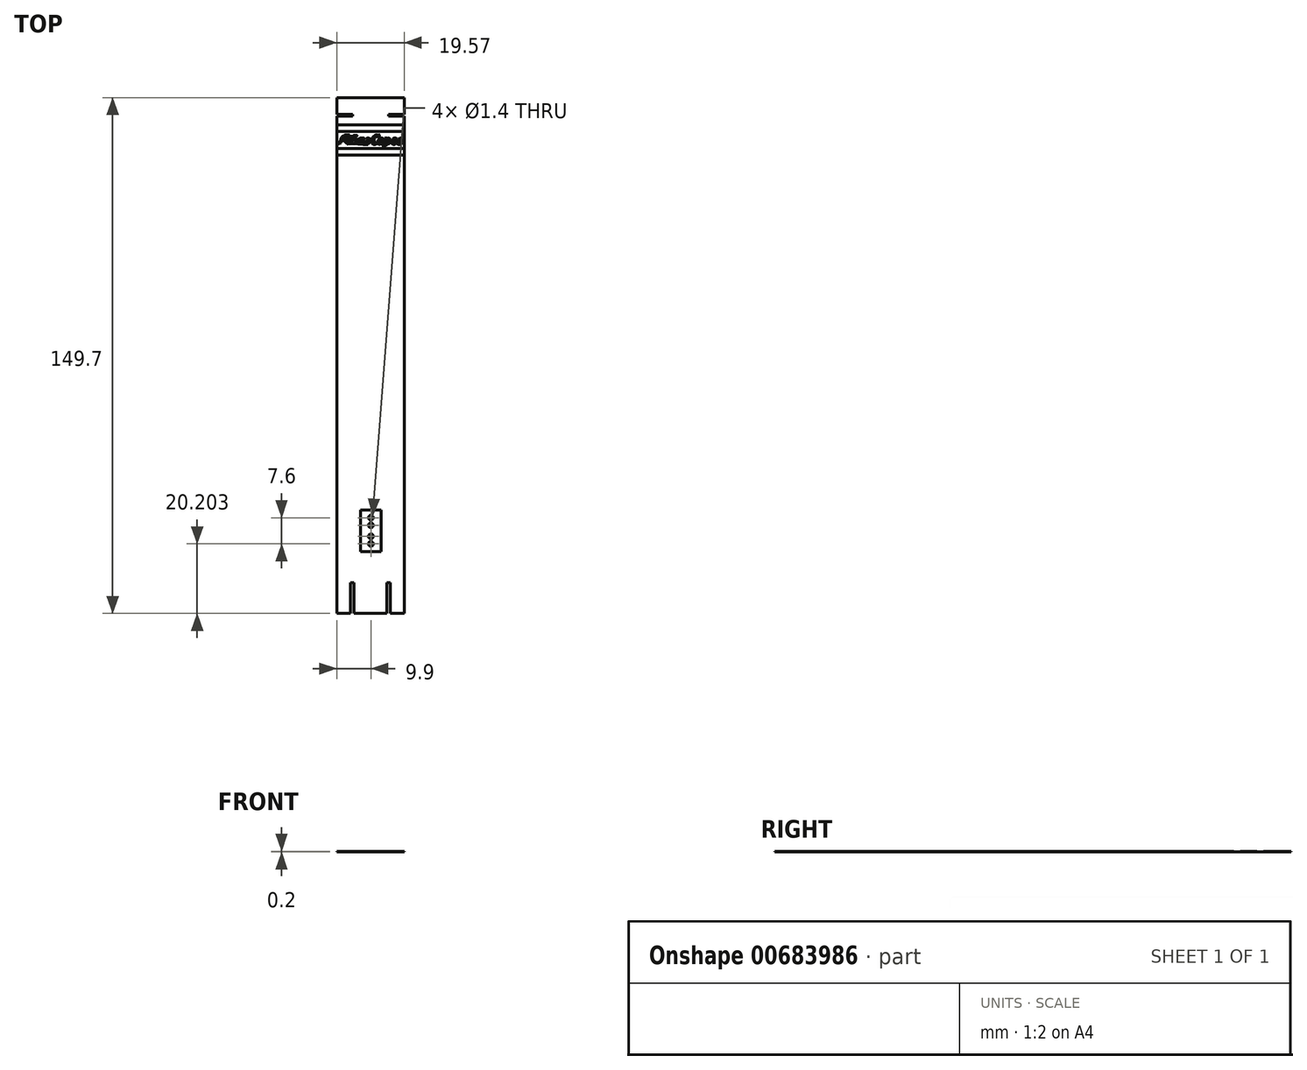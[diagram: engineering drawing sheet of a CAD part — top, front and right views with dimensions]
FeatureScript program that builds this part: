
annotation { "Feature Type Name" : "Feature", "Feature Type Description" : "" }
export const myFeature = defineFeature(function(context is Context, id is Id, definition is map)
    precondition{}
    {
        {
            var Q0;
            Q0=qCreatedBy(makeId("Top.planeOp"),FACE);
            var sketch = newSketch(context, id + "F0", { "sketchPlane" : qUnion([Q0])});
            skLineSegment(sketch, "E0.bottom", {"start": v(0, -51.23) * mm, "end": v(-19.57, -51.23) * mm});
            skLineSegment(sketch, "E0.top", {"start": v(0, 98.47) * mm, "end": v(-19.57, 98.47) * mm});
            skLineSegment(sketch, "E0.left", {"start": v(0, -51.23) * mm, "end": v(0, 98.47) * mm});
            skLineSegment(sketch, "E0.right", {"start": v(-19.57, -51.23) * mm, "end": v(-19.57, 98.47) * mm});
            skSolve(sketch);
        }
        {
            var Q0;
            Q0=makeQuery(id+"F0.imprint","IMPRINT",FACE,{"disambiguationData":[TD([[makeQuery(id+"F0.imprint","IMPRINT",EDGE,{"derivedFrom":sQuery(id+"F0.wireOp",EDGE,"E0.bottom")}),-1.0]])]});
            extrude(context, id + "F1", {"entities" : qUnion([Q0]), "depth" : 0.2 * mm, "offsetDistance" : 25 * mm});
        }
        {
            var Q0;
            Q0=makeQuery(id+"F1.opExtrude","CAP_FACE",FACE,{"disambiguationData":[OSD([sQuery(id+"F0.wireOp",EDGE,"E0.bottom"),sQuery(id+"F0.wireOp",EDGE,"E0.top"),sQuery(id+"F0.wireOp",EDGE,"E0.left"),sQuery(id+"F0.wireOp",EDGE,"E0.right")])],"isStart":false});
            var sketch = newSketch(context, id + "F2", { "sketchPlane" : qUnion([Q0])});
            skLineSegment(sketch, "E1", {"start": v(0, 90.56) * mm, "end": v(-19.57, 90.56) * mm});
            skLineSegment(sketch, "E2", {"start": v(-19.57, 90.56) * mm, "end": v(-19.57, 88.66) * mm});
            skLineSegment(sketch, "E3", {"start": v(-19.57, 88.66) * mm, "end": v(0, 88.66) * mm});
            skLineSegment(sketch, "E4", {"start": v(0, 88.66) * mm, "end": v(0, 90.56) * mm});
            skLineSegment(sketch, "E5", {"start": v(0, 88.66) * mm, "end": v(0, 83.76) * mm});
            skLineSegment(sketch, "E6", {"start": v(0, 83.76) * mm, "end": v(-19.57, 83.76) * mm});
            skLineSegment(sketch, "E7", {"start": v(-19.57, 83.76) * mm, "end": v(-19.57, 81.86) * mm});
            skLineSegment(sketch, "E8", {"start": v(-19.57, 81.86) * mm, "end": v(0, 81.86) * mm});
            skLineSegment(sketch, "E9", {"start": v(0, 81.86) * mm, "end": v(0, 83.76) * mm});
            skSolve(sketch);
        }
        {
            var Q0;
            Q0 = qSketchRegion(id + "F2", true);
            extrude(context, id + "F3", {"entities" : qUnion([Q0]), "operationType" : NewBodyOperationType.REMOVE, "oppositeDirection" : true, "depth" : 0.1 * mm, "offsetDistance" : 25 * mm});
        }
        {
            var Q0;
            {var subQ0=sQuery(id+"F0.wireOp",EDGE,"E0.top");var subQ1=sQuery(id+"F0.wireOp",EDGE,"E0.left");var subQ2=sQuery(id+"F0.wireOp",EDGE,"E0.right");Q0=makeQuery(id+"F3.boolean.opBoolean","SPLIT",FACE,{"disambiguationData":[TD([makeQuery(id+"F1.opExtrude","SWEPT_FACE",FACE,{"disambiguationData":[OSD([subQ0])]})])],"derivedFrom":makeQuery(id+"F1.opExtrude","CAP_FACE",FACE,{"disambiguationData":[OSD([sQuery(id+"F0.wireOp",EDGE,"E0.bottom"),subQ0,subQ1,subQ2])],"isStart":false})});}
            var sketch = newSketch(context, id + "F4", { "sketchPlane" : qUnion([Q0])});
            skLineSegment(sketch, "E10", {"start": v(0, 93.57) * mm, "end": v(-4.6, 93.57) * mm});
            skLineSegment(sketch, "E11", {"start": v(-4.6, 93.57) * mm, "end": v(-4.6, 93.07) * mm});
            skLineSegment(sketch, "E12", {"start": v(-4.6, 93.07) * mm, "end": v(0, 93.07) * mm});
            skLineSegment(sketch, "E13", {"start": v(-19.57, 93.57) * mm, "end": v(-14.97, 93.57) * mm});
            skLineSegment(sketch, "E14", {"start": v(-14.97, 93.57) * mm, "end": v(-14.97, 93.07) * mm});
            skLineSegment(sketch, "E15", {"start": v(-14.97, 93.07) * mm, "end": v(-19.57, 93.07) * mm});
            skLineSegment(sketch, "E16", {"start": v(-19.57, 93.57) * mm, "end": v(-19.57, 93.07) * mm});
            skLineSegment(sketch, "E17", {"start": v(0, 93.57) * mm, "end": v(0, 93.07) * mm});
            skSolve(sketch);
        }
        {
            var Q0;
            Q0=makeQuery(id+"F4.imprint","IMPRINT",FACE,{"disambiguationData":[TD([[makeQuery(id+"F4.imprint","IMPRINT",EDGE,{"derivedFrom":sQuery(id+"F4.wireOp",EDGE,"E13")}),-1.0]])]});
            var Q1;
            Q1=makeQuery(id+"F4.imprint","IMPRINT",FACE,{"disambiguationData":[TD([[makeQuery(id+"F4.imprint","IMPRINT",EDGE,{"derivedFrom":sQuery(id+"F4.wireOp",EDGE,"E10")}),1.0]])]});
            extrude(context, id + "F5", {"entities" : qUnion([Q0, Q1]), "operationType" : NewBodyOperationType.REMOVE, "oppositeDirection" : true, "depth" : 0.2 * mm, "offsetDistance" : 25 * mm});
        }
        {
            var Q0;
            {var subQ0=sQuery(id+"F0.wireOp",EDGE,"E0.left");var subQ1=sQuery(id+"F0.wireOp",EDGE,"E0.right");Q0=makeQuery(id+"F3.boolean.opBoolean","SPLIT",FACE,{"disambiguationData":[TD([makeQuery(id+"F3.opExtrude","SWEPT_FACE",FACE,{"disambiguationData":[OSD([sQuery(id+"F2.wireOp",EDGE,"E3")])]})])],"derivedFrom":makeQuery(id+"F1.opExtrude","CAP_FACE",FACE,{"disambiguationData":[OSD([sQuery(id+"F0.wireOp",EDGE,"E0.bottom"),sQuery(id+"F0.wireOp",EDGE,"E0.top"),subQ0,subQ1])],"isStart":false})});}
            var sketch = newSketch(context, id + "F6", { "sketchPlane" : qUnion([Q0])});
            skFitSpline(sketch, "E18", {"points": [v(-19.42, 85.15) * mm, v(-19.42, 84.95) * mm, v(-19.42, 84.87) * mm, v(-19.22, 84.83) * mm, v(-19.09, 84.82) * mm, v(-18.87, 84.84) * mm, v(-18.7, 84.9) * mm, v(-18.52, 84.98) * mm, v(-18.35, 85.1) * mm, v(-18.2, 85.24) * mm, v(-18.12, 85.38) * mm, v(-18, 85.53) * mm, v(-17.94, 85.73) * mm, v(-17.89, 85.92) * mm, v(-17.86, 86.08) * mm, v(-17.85, 86.1) * mm, v(-17.71, 86.1) * mm, v(-17.6, 86.1) * mm, v(-17.46, 86.1) * mm, v(-17.32, 86.08) * mm, v(-17.3, 86.08) * mm, v(-17.26, 86.1) * mm, v(-17.43, 85.47) * mm, v(-17.45, 85.37) * mm, v(-17.44, 85.2) * mm, v(-17.4, 85.1) * mm, v(-17.35, 85.01) * mm, v(-17.29, 84.94) * mm, v(-17.22, 84.9) * mm, v(-17.16, 84.87) * mm, v(-17.02, 84.84) * mm, v(-16.85, 84.84) * mm, v(-16.7, 84.84) * mm, v(-16.55, 84.88) * mm, v(-16.42, 84.92) * mm, v(-16.33, 85.01) * mm, v(-16.26, 85.07) * mm, v(-16.19, 85.15) * mm, v(-16.15, 85.18) * mm, v(-16.13, 85.19) * mm, v(-16.08, 85.1) * mm, v(-16.03, 84.97) * mm, v(-15.98, 84.9) * mm, v(-15.9, 84.84) * mm, v(-15.75, 84.84) * mm, v(-15.6, 84.83) * mm, v(-15.55, 84.83) * mm, v(-15.46, 84.85) * mm, v(-15.4, 84.88) * mm, v(-15.3, 84.91) * mm, v(-15.23, 84.94) * mm, v(-15.1, 85.04) * mm, v(-15, 85.1) * mm, v(-14.97, 85.17) * mm, v(-14.93, 85.18) * mm, v(-14.89, 85.22) * mm, v(-14.83, 85.12) * mm, v(-14.81, 85.02) * mm, v(-14.77, 84.95) * mm, v(-14.75, 84.93) * mm, v(-14.62, 84.87) * mm, v(-14.55, 84.87) * mm, v(-14.45, 84.85) * mm, v(-14.34, 84.85) * mm, v(-14.27, 84.86) * mm, v(-14.21, 84.9) * mm, v(-14.1, 84.94) * mm, v(-13.98, 85) * mm, v(-13.92, 85.05) * mm, v(-13.85, 85.12) * mm, v(-13.78, 85.16) * mm, v(-13.73, 85.22) * mm, v(-13.7, 85.23) * mm, v(-13.6, 85.3) * mm, v(-13.58, 85.29) * mm, v(-13.56, 85.15) * mm, v(-13.49, 85.05) * mm, v(-13.45, 85.02) * mm, v(-13.4, 84.97) * mm, v(-13.34, 84.94) * mm, v(-13.25, 84.89) * mm, v(-13.21, 84.89) * mm, v(-13.13, 84.86) * mm, v(-13.04, 84.88) * mm, v(-12.99, 84.87) * mm, v(-12.9, 84.88) * mm, v(-12.86, 84.9) * mm, v(-12.78, 84.9) * mm, v(-12.73, 84.93) * mm, v(-12.69, 84.96) * mm, v(-12.66, 85) * mm, v(-12.59, 85.05) * mm, v(-12.56, 85.1) * mm, v(-12.51, 85.12) * mm, v(-12.46, 85.13) * mm, v(-12.45, 85.09) * mm, v(-12.42, 85.01) * mm, v(-12.37, 84.96) * mm, v(-12.34, 84.93) * mm, v(-12.3, 84.9) * mm, v(-12.24, 84.89) * mm, v(-12.17, 84.87) * mm, v(-12.08, 84.87) * mm, v(-12.01, 84.87) * mm, v(-11.93, 84.88) * mm, v(-11.88, 84.89) * mm, v(-11.83, 84.92) * mm, v(-11.77, 84.96) * mm, v(-11.72, 84.99) * mm, v(-11.68, 85.04) * mm, v(-11.64, 85.06) * mm, v(-11.6, 85.1) * mm, v(-11.54, 85.11) * mm, v(-11.5, 85.17) * mm, v(-11.47, 85.18) * mm, v(-11.43, 85.16) * mm, v(-11.4, 85.08) * mm, v(-11.38, 85.04) * mm, v(-11.33, 85) * mm, v(-11.25, 84.97) * mm, v(-11.2, 84.93) * mm, v(-11.12, 84.9) * mm, v(-11.07, 84.88) * mm, v(-11.02, 84.87) * mm, v(-10.95, 84.86) * mm, v(-10.88, 84.84) * mm, v(-10.8, 84.83) * mm, v(-10.7, 84.8) * mm, v(-10.65, 84.83) * mm, v(-10.6, 84.85) * mm, v(-10.51, 84.87) * mm, v(-10.3, 85.02) * mm, v(-10.25, 85.07) * mm, v(-10.2, 85.12) * mm, v(-10.16, 85.15) * mm, v(-10.13, 85.2) * mm, v(-10.1, 85.22) * mm, v(-10.06, 85.28) * mm, v(-10.04, 85.32) * mm, v(-10.03, 85.35) * mm, v(-10.03, 85.43) * mm, v(-10.01, 85.49) * mm, v(-10.03, 85.54) * mm, v(-10.04, 85.58) * mm, v(-10.05, 85.62) * mm, v(-10.06, 85.67) * mm, v(-10.08, 85.72) * mm, v(-10.11, 85.75) * mm, v(-10.17, 85.8) * mm, v(-10.19, 85.83) * mm, v(-10.23, 85.87) * mm, v(-10.3, 85.9) * mm, v(-10.33, 85.93) * mm, v(-10.4, 85.97) * mm, v(-10.47, 86) * mm, v(-10.5, 86.04) * mm, v(-10.55, 86.09) * mm, v(-10.62, 86.14) * mm, v(-10.67, 86.18) * mm, v(-10.7, 86.29) * mm, v(-10.7, 86.34) * mm, v(-10.68, 86.4) * mm, v(-10.66, 86.46) * mm, v(-10.62, 86.5) * mm, v(-10.58, 86.53) * mm, v(-10.56, 86.56) * mm, v(-10.53, 86.56) * mm, v(-10.5, 86.56) * mm, v(-10.43, 86.55) * mm, v(-10.4, 86.55) * mm, v(-10.34, 86.55) * mm, v(-10.32, 86.55) * mm, v(-10.3, 86.51) * mm, v(-10.31, 86.47) * mm, v(-10.3, 86.43) * mm, v(-10.32, 86.4) * mm, v(-10.33, 86.39) * mm, v(-10.35, 86.37) * mm, v(-10.36, 86.34) * mm, v(-10.36, 86.32) * mm, v(-10.35, 86.28) * mm, v(-10.35, 86.24) * mm, v(-10.33, 86.2) * mm, v(-10.31, 86.17) * mm, v(-10.28, 86.14) * mm, v(-10.25, 86.12) * mm, v(-10.2, 86.1) * mm, v(-10.17, 86.1) * mm, v(-10.13, 86.1) * mm, v(-10.08, 86.12) * mm, v(-10.04, 86.13) * mm, v(-10.01, 86.15) * mm, v(-9.98, 86.18) * mm, v(-9.95, 86.2) * mm, v(-9.93, 86.22) * mm, v(-9.92, 86.25) * mm, v(-9.91, 86.29) * mm, v(-9.9, 86.33) * mm, v(-9.9, 86.36) * mm, v(-9.9, 86.4) * mm, v(-9.9, 86.45) * mm, v(-9.92, 86.47) * mm, v(-9.93, 86.5) * mm, v(-9.95, 86.55) * mm, v(-9.98, 86.58) * mm, v(-10, 86.6) * mm, v(-10.03, 86.63) * mm, v(-10.06, 86.66) * mm, v(-10.1, 86.68) * mm, v(-10.14, 86.7) * mm, v(-10.18, 86.72) * mm, v(-10.2, 86.73) * mm, v(-10.24, 86.75) * mm, v(-10.28, 86.76) * mm, v(-10.32, 86.77) * mm, v(-10.37, 86.77) * mm, v(-10.43, 86.77) * mm, v(-10.5, 86.77) * mm, v(-10.56, 86.77) * mm, v(-10.6, 86.76) * mm, v(-10.63, 86.76) * mm, v(-10.68, 86.75) * mm, v(-10.72, 86.75) * mm, v(-10.78, 86.74) * mm, v(-10.8, 86.73) * mm, v(-10.84, 86.7) * mm, v(-10.87, 86.69) * mm, v(-10.9, 86.66) * mm, v(-10.93, 86.62) * mm, v(-10.96, 86.6) * mm, v(-11, 86.55) * mm, v(-11.02, 86.53) * mm, v(-11.1, 86.5) * mm, v(-11.17, 86.39) * mm, v(-11.19, 86.35) * mm, v(-11.2, 86.26) * mm, v(-11.2, 86.18) * mm, v(-11.2, 86.1) * mm, v(-11.19, 86.02) * mm, v(-11.16, 85.95) * mm, v(-11.13, 85.92) * mm, v(-11.12, 85.89) * mm, v(-11.03, 85.8) * mm, v(-10.97, 85.75) * mm, v(-10.9, 85.68) * mm, v(-10.85, 85.65) * mm, v(-10.82, 85.62) * mm, v(-10.75, 85.6) * mm, v(-10.72, 85.58) * mm, v(-10.68, 85.54) * mm, v(-10.66, 85.48) * mm, v(-10.64, 85.44) * mm, v(-10.63, 85.4) * mm, v(-10.61, 85.3) * mm, v(-10.62, 85.24) * mm, v(-10.64, 85.18) * mm, v(-10.68, 85.15) * mm, v(-10.72, 85.12) * mm, v(-10.78, 85.1) * mm, v(-10.83, 85.07) * mm, v(-10.88, 85.07) * mm, v(-10.95, 85.07) * mm, v(-10.99, 85.07) * mm, v(-11.05, 85.09) * mm, v(-11.09, 85.1) * mm, v(-11.11, 85.12) * mm, v(-11.16, 85.14) * mm, v(-11.17, 85.15) * mm, v(-11.2, 85.18) * mm, v(-11.22, 85.2) * mm, v(-11.23, 85.28) * mm, v(-11.22, 85.3) * mm, v(-11.2, 85.32) * mm, v(-11.18, 85.33) * mm, v(-11.15, 85.33) * mm, v(-11.13, 85.34) * mm, v(-11.11, 85.34) * mm, v(-11.1, 85.36) * mm, v(-11.09, 85.43) * mm, v(-11.09, 85.48) * mm, v(-11.1, 85.52) * mm, v(-11.09, 85.58) * mm, v(-11.1, 85.6) * mm, v(-11.1, 85.63) * mm, v(-11.12, 85.64) * mm, v(-11.14, 85.66) * mm, v(-11.2, 85.68) * mm, v(-11.23, 85.7) * mm, v(-11.29, 85.7) * mm, v(-11.33, 85.7) * mm, v(-11.4, 85.69) * mm, v(-11.42, 85.66) * mm, v(-11.46, 85.62) * mm, v(-11.48, 85.6) * mm, v(-11.49, 85.56) * mm, v(-11.5, 85.54) * mm, v(-11.51, 85.51) * mm, v(-11.51, 85.47) * mm, v(-11.52, 85.45) * mm, v(-11.54, 85.39) * mm, v(-11.54, 85.35) * mm, v(-11.57, 85.3) * mm, v(-11.6, 85.3) * mm, v(-11.63, 85.26) * mm, v(-11.67, 85.23) * mm, v(-11.7, 85.22) * mm, v(-11.7, 85.22) * mm, v(-11.72, 85.21) * mm, v(-11.77, 85.21) * mm, v(-11.8, 85.21) * mm, v(-11.85, 85.22) * mm, v(-11.87, 85.23) * mm, v(-11.9, 85.24) * mm, v(-11.91, 85.25) * mm, v(-11.93, 85.28) * mm, v(-11.94, 85.31) * mm, v(-11.93, 85.37) * mm, v(-11.93, 85.44) * mm, v(-11.9, 85.5) * mm, v(-11.9, 85.56) * mm, v(-11.89, 85.6) * mm, v(-11.88, 85.67) * mm, v(-11.87, 85.7) * mm, v(-11.87, 85.75) * mm, v(-11.84, 85.82) * mm, v(-11.83, 85.87) * mm, v(-11.81, 85.9) * mm, v(-11.8, 85.95) * mm, v(-11.79, 85.99) * mm, v(-11.78, 86.02) * mm, v(-11.77, 86.08) * mm, v(-11.67, 86.5) * mm, v(-11.67, 86.55) * mm, v(-11.65, 86.59) * mm, v(-11.64, 86.6) * mm, v(-11.62, 86.65) * mm, v(-11.62, 86.68) * mm, v(-11.62, 86.7) * mm, v(-11.64, 86.7) * mm, v(-11.67, 86.7) * mm, v(-11.73, 86.71) * mm, v(-11.8, 86.71) * mm, v(-11.84, 86.71) * mm, v(-11.9, 86.71) * mm, v(-11.92, 86.71) * mm, v(-11.96, 86.7) * mm, v(-12, 86.7) * mm, v(-12.05, 86.71) * mm, v(-12.1, 86.7) * mm, v(-12.1, 86.7) * mm, v(-12.12, 86.7) * mm, v(-12.13, 86.7) * mm, v(-12.14, 86.7) * mm, v(-12.16, 86.69) * mm, v(-12.16, 86.66) * mm, v(-12.17, 86.6) * mm, v(-12.17, 86.58) * mm, v(-12.18, 86.57) * mm, v(-12.2, 86.56) * mm, v(-12.21, 86.58) * mm, v(-12.23, 86.6) * mm, v(-12.25, 86.62) * mm, v(-12.27, 86.64) * mm, v(-12.3, 86.65) * mm, v(-12.34, 86.68) * mm, v(-12.38, 86.7) * mm, v(-12.4, 86.7) * mm, v(-12.44, 86.72) * mm, v(-12.47, 86.73) * mm, v(-12.5, 86.73) * mm, v(-12.54, 86.73) * mm, v(-12.6, 86.74) * mm, v(-12.66, 86.75) * mm, v(-12.7, 86.74) * mm, v(-12.74, 86.74) * mm, v(-12.78, 86.74) * mm, v(-12.81, 86.73) * mm, v(-13.1, 86.55) * mm, v(-13.24, 86.42) * mm, v(-13.33, 86.32) * mm, v(-13.4, 86.22) * mm, v(-13.53, 85.99) * mm, v(-13.66, 85.76) * mm, v(-13.76, 85.57) * mm, v(-13.85, 85.45) * mm, v(-13.92, 85.36) * mm, v(-13.97, 85.3) * mm, v(-14.04, 85.27) * mm, v(-14.1, 85.26) * mm, v(-14.15, 85.26) * mm, v(-14.18, 85.26) * mm, v(-14.21, 85.27) * mm, v(-14.22, 85.36) * mm, v(-14.2, 85.53) * mm, v(-14.14, 85.65) * mm, v(-14.09, 85.94) * mm, v(-14.04, 86.12) * mm, v(-13.96, 86.4) * mm, v(-13.9, 86.67) * mm, v(-13.87, 86.8) * mm, v(-13.85, 86.88) * mm, v(-13.81, 87.1) * mm, v(-13.8, 87.13) * mm, v(-13.76, 87.22) * mm, v(-13.76, 87.27) * mm, v(-13.74, 87.32) * mm, v(-13.72, 87.35) * mm, v(-13.71, 87.45) * mm, v(-13.71, 87.5) * mm, v(-13.71, 87.53) * mm, v(-13.89, 87.53) * mm, v(-14.11, 87.53) * mm, v(-14.17, 87.53) * mm, v(-14.24, 87.54) * mm, v(-14.37, 87.54) * mm, v(-14.47, 87.54) * mm, v(-14.5, 87.54) * mm, v(-14.53, 87.54) * mm, v(-14.58, 87.54) * mm, v(-14.64, 87.54) * mm, v(-14.66, 87.54) * mm, v(-14.69, 87.52) * mm, v(-14.68, 87.46) * mm, v(-14.68, 87.4) * mm, v(-14.69, 87.35) * mm, v(-14.65, 87.35) * mm, v(-14.57, 87.35) * mm, v(-14.47, 87.35) * mm, v(-14.4, 87.34) * mm, v(-14.33, 87.33) * mm, v(-14.36, 87.21) * mm, v(-14.37, 87.12) * mm, v(-14.38, 87.04) * mm, v(-14.4, 86.93) * mm, v(-14.42, 86.86) * mm, v(-14.45, 86.78) * mm, v(-14.48, 86.64) * mm, v(-14.5, 86.53) * mm, v(-14.54, 86.43) * mm, v(-14.56, 86.3) * mm, v(-14.58, 86.17) * mm, v(-14.6, 86.1) * mm, v(-14.63, 85.98) * mm, v(-14.66, 85.9) * mm, v(-14.7, 85.78) * mm, v(-14.73, 85.69) * mm, v(-14.77, 85.62) * mm, v(-14.85, 85.47) * mm, v(-14.96, 85.43) * mm, v(-15.03, 85.37) * mm, v(-15.07, 85.36) * mm, v(-15.14, 85.32) * mm, v(-15.2, 85.28) * mm, v(-15.27, 85.27) * mm, v(-15.32, 85.26) * mm, v(-15.37, 85.25) * mm, v(-15.44, 85.27) * mm, v(-15.47, 85.28) * mm, v(-15.5, 85.3) * mm, v(-15.5, 85.38) * mm, v(-15.5, 85.5) * mm, v(-15.49, 85.57) * mm, v(-15.46, 85.7) * mm, v(-15.46, 85.78) * mm, v(-15.43, 85.89) * mm, v(-15.4, 86) * mm, v(-15.38, 86.1) * mm, v(-15.36, 86.18) * mm, v(-15.33, 86.34) * mm, v(-15.32, 86.43) * mm, v(-15.3, 86.48) * mm, v(-15.28, 86.52) * mm, v(-15.2, 86.53) * mm, v(-15.14, 86.53) * mm, v(-15.07, 86.52) * mm, v(-15, 86.52) * mm, v(-14.94, 86.51) * mm, v(-14.88, 86.5) * mm, v(-14.86, 86.5) * mm, v(-14.85, 86.51) * mm, v(-14.84, 86.6) * mm, v(-14.83, 86.65) * mm, v(-14.82, 86.69) * mm, v(-14.83, 86.71) * mm, v(-14.9, 86.73) * mm, v(-15, 86.74) * mm, v(-15.04, 86.74) * mm, v(-15.1, 86.73) * mm, v(-15.18, 86.73) * mm, v(-15.2, 86.73) * mm, v(-15.22, 86.77) * mm, v(-15.21, 86.8) * mm, v(-15.19, 86.86) * mm, v(-15.18, 86.9) * mm, v(-15.1, 87.24) * mm, v(-15.1, 87.28) * mm, v(-15.16, 87.28) * mm, v(-15.2, 87.28) * mm, v(-15.25, 87.28) * mm, v(-15.31, 87.28) * mm, v(-15.34, 87.27) * mm, v(-15.36, 87.19) * mm, v(-15.4, 87.14) * mm, v(-15.42, 87.1) * mm, v(-15.45, 87.05) * mm, v(-15.52, 86.98) * mm, v(-15.56, 86.93) * mm, v(-15.6, 86.89) * mm, v(-15.64, 86.85) * mm, v(-15.68, 86.81) * mm, v(-15.75, 86.77) * mm, v(-15.78, 86.77) * mm, v(-15.85, 86.75) * mm, v(-15.9, 86.73) * mm, v(-15.97, 86.73) * mm, v(-16.03, 86.74) * mm, v(-16.07, 86.74) * mm, v(-16.11, 86.74) * mm, v(-16.13, 86.73) * mm, v(-16.15, 86.68) * mm, v(-16.15, 86.63) * mm, v(-16.17, 86.6) * mm, v(-16.17, 86.53) * mm, v(-16.16, 86.51) * mm, v(-16.14, 86.52) * mm, v(-16.06, 86.5) * mm, v(-15.99, 86.5) * mm, v(-15.95, 86.5) * mm, v(-15.89, 86.5) * mm, v(-15.87, 86.5) * mm, v(-15.86, 86.4) * mm, v(-15.88, 86.33) * mm, v(-15.9, 86.29) * mm, v(-15.92, 86.22) * mm, v(-15.96, 86.08) * mm, v(-15.96, 86.04) * mm, v(-16, 85.95) * mm, v(-16.03, 85.87) * mm, v(-16.07, 85.8) * mm, v(-16.1, 85.74) * mm, v(-16.15, 85.65) * mm, v(-16.17, 85.6) * mm, v(-16.23, 85.52) * mm, v(-16.27, 85.46) * mm, v(-16.3, 85.4) * mm, v(-16.33, 85.35) * mm, v(-16.41, 85.3) * mm, v(-16.47, 85.23) * mm, v(-16.52, 85.2) * mm, v(-16.56, 85.18) * mm, v(-16.63, 85.17) * mm, v(-16.68, 85.18) * mm, v(-16.74, 85.2) * mm, v(-16.78, 85.21) * mm, v(-16.8, 85.23) * mm, v(-16.81, 85.3) * mm, v(-16.82, 85.4) * mm, v(-16.8, 85.46) * mm, v(-16.8, 85.54) * mm, v(-16.77, 85.65) * mm, v(-16.75, 85.72) * mm, v(-16.72, 85.84) * mm, v(-16.67, 85.93) * mm, v(-16.66, 86.04) * mm, v(-16.64, 86.12) * mm, v(-16.63, 86.18) * mm, v(-16.62, 86.27) * mm, v(-16.6, 86.34) * mm, v(-16.58, 86.4) * mm, v(-16.55, 86.45) * mm, v(-16.53, 86.52) * mm, v(-16.46, 86.77) * mm, v(-16.45, 86.89) * mm, v(-16.41, 86.96) * mm, v(-16.38, 87.07) * mm, v(-16.37, 87.14) * mm, v(-16.36, 87.19) * mm, v(-16.34, 87.25) * mm, v(-16.32, 87.33) * mm, v(-16.3, 87.39) * mm, v(-16.29, 87.44) * mm, v(-16.24, 87.45) * mm, v(-16.18, 87.46) * mm, v(-16.1, 87.47) * mm, v(-16.02, 87.47) * mm, v(-15.94, 87.47) * mm, v(-15.9, 87.48) * mm, v(-15.89, 87.48) * mm], "startDerivative": vector(4.7, -73.51) * mm, "endDerivative": vector(13.13, -1.63) * mm});
            skFitSpline(sketch, "E19", {"points": [v(-15.89, 87.48) * mm, v(-15.89, 87.57) * mm, v(-15.86, 87.62) * mm, v(-15.89, 87.64) * mm, v(-15.94, 87.65) * mm, v(-16.08, 87.65) * mm, v(-16.28, 87.66) * mm, v(-16.51, 87.66) * mm, v(-16.7, 87.66) * mm, v(-16.9, 87.66) * mm, v(-17.05, 87.63) * mm, v(-17.2, 87.6) * mm, v(-17.28, 87.57) * mm, v(-17.37, 87.54) * mm, v(-17.45, 87.48) * mm, v(-17.52, 87.48) * mm, v(-17.56, 87.43) * mm, v(-17.64, 87.4) * mm, v(-17.7, 87.35) * mm, v(-17.76, 87.3) * mm, v(-17.8, 87.27) * mm, v(-17.84, 87.24) * mm, v(-17.88, 87.2) * mm, v(-17.95, 87.13) * mm, v(-17.99, 87.07) * mm, v(-18.05, 87.01) * mm, v(-18.1, 86.95) * mm, v(-18.19, 86.8) * mm, v(-18.24, 86.73) * mm, v(-18.28, 86.64) * mm, v(-18.37, 86.45) * mm, v(-18.4, 86.35) * mm, v(-18.44, 86.24) * mm, v(-18.48, 86.1) * mm, v(-18.5, 86.01) * mm, v(-18.5, 85.88) * mm, v(-18.54, 85.8) * mm, v(-18.55, 85.76) * mm, v(-18.57, 85.65) * mm, v(-18.6, 85.54) * mm, v(-18.64, 85.47) * mm, v(-18.67, 85.4) * mm, v(-18.7, 85.33) * mm, v(-18.74, 85.27) * mm, v(-18.8, 85.2) * mm, v(-18.84, 85.16) * mm, v(-18.9, 85.12) * mm, v(-18.98, 85.08) * mm, v(-19.03, 85.06) * mm, v(-19.12, 85.05) * mm, v(-19.2, 85.05) * mm, v(-19.25, 85.05) * mm, v(-19.32, 85.07) * mm, v(-19.34, 85.08) * mm, v(-19.37, 85.11) * mm, v(-19.39, 85.14) * mm, v(-19.42, 85.15) * mm], "startDerivative": vector(-1.11, 5.38) * mm, "endDerivative": vector(-3.21, 0.45) * mm});
            skFitSpline(sketch, "E20", {"points": [v(-17.75, 86.29) * mm, v(-17.6, 86.27) * mm, v(-17.43, 86.27) * mm, v(-17.27, 86.26) * mm, v(-17.22, 86.27) * mm, v(-17.17, 86.33) * mm, v(-17.12, 86.52) * mm, v(-17.06, 86.73) * mm, v(-17.03, 86.85) * mm, v(-17, 87) * mm, v(-16.98, 87.05) * mm, v(-16.95, 87.13) * mm, v(-16.94, 87.21) * mm, v(-16.9, 87.28) * mm, v(-16.89, 87.4) * mm, v(-16.9, 87.41) * mm, v(-16.99, 87.42) * mm, v(-17.07, 87.42) * mm, v(-17.16, 87.4) * mm, v(-17.24, 87.36) * mm, v(-17.3, 87.31) * mm, v(-17.35, 87.26) * mm, v(-17.4, 87.21) * mm, v(-17.43, 87.13) * mm, v(-17.47, 87.09) * mm, v(-17.5, 87.02) * mm, v(-17.55, 86.94) * mm, v(-17.58, 86.9) * mm, v(-17.62, 86.81) * mm, v(-17.64, 86.77) * mm, v(-17.68, 86.7) * mm, v(-17.7, 86.64) * mm, v(-17.74, 86.55) * mm, v(-17.77, 86.48) * mm, v(-17.79, 86.4) * mm, v(-17.8, 86.34) * mm, v(-17.75, 86.29) * mm]});
            skFitSpline(sketch, "E21", {"points": [v(-12.78, 85.21) * mm, v(-12.72, 85.23) * mm, v(-12.63, 85.26) * mm, v(-12.6, 85.26) * mm, v(-12.58, 85.33) * mm, v(-12.55, 85.4) * mm, v(-12.53, 85.4) * mm, v(-12.5, 85.47) * mm, v(-12.47, 85.5) * mm, v(-12.47, 85.53) * mm, v(-12.46, 85.6) * mm, v(-12.44, 85.62) * mm, v(-12.44, 85.68) * mm, v(-12.43, 85.71) * mm, v(-12.41, 85.78) * mm, v(-12.4, 85.83) * mm, v(-12.4, 85.9) * mm, v(-12.39, 85.94) * mm, v(-12.36, 85.99) * mm, v(-12.35, 86.1) * mm, v(-12.35, 86.13) * mm, v(-12.35, 86.2) * mm, v(-12.35, 86.27) * mm, v(-12.36, 86.34) * mm, v(-12.37, 86.4) * mm, v(-12.4, 86.4) * mm, v(-12.43, 86.45) * mm, v(-12.48, 86.46) * mm, v(-12.53, 86.48) * mm, v(-12.6, 86.48) * mm, v(-12.62, 86.48) * mm, v(-12.67, 86.46) * mm, v(-12.7, 86.4) * mm, v(-12.75, 86.34) * mm, v(-12.79, 86.29) * mm, v(-12.83, 86.27) * mm, v(-12.85, 86.2) * mm, v(-12.88, 86.1) * mm, v(-12.91, 86.07) * mm, v(-12.95, 85.99) * mm, v(-12.97, 85.93) * mm, v(-13, 85.84) * mm, v(-13, 85.78) * mm, v(-13.02, 85.67) * mm, v(-13.01, 85.6) * mm, v(-13.01, 85.47) * mm, v(-13, 85.4) * mm, v(-12.98, 85.33) * mm, v(-12.96, 85.33) * mm, v(-12.92, 85.27) * mm, v(-12.9, 85.27) * mm, v(-12.86, 85.23) * mm, v(-12.83, 85.23) * mm, v(-12.78, 85.21) * mm]});
            skFitSpline(sketch, "E22", {"points": [v(-7.57, 86.72) * mm, v(-7.37, 86.73) * mm, v(-7.33, 86.93) * mm, v(-7.29, 87.04) * mm, v(-7.29, 87.15) * mm, v(-7.27, 87.2) * mm, v(-7.25, 87.29) * mm, v(-7.22, 87.35) * mm, v(-7.2, 87.43) * mm, v(-7.2, 87.49) * mm, v(-7.16, 87.57) * mm, v(-7.16, 87.66) * mm, v(-7.28, 87.64) * mm, v(-7.32, 87.64) * mm, v(-7.37, 87.64) * mm, v(-7.4, 87.6) * mm, v(-7.43, 87.55) * mm, v(-7.44, 87.52) * mm, v(-7.48, 87.5) * mm, v(-7.52, 87.5) * mm, v(-7.54, 87.5) * mm], "startDerivative": vector(3, -0.58) * mm, "endDerivative": vector(-0.64, 0.06) * mm});
            skFitSpline(sketch, "E23", {"points": [v(-7.54, 87.5) * mm, v(-7.59, 87.56) * mm, v(-7.67, 87.59) * mm, v(-7.7, 87.61) * mm, v(-7.78, 87.64) * mm, v(-7.84, 87.66) * mm, v(-7.93, 87.67) * mm, v(-8, 87.67) * mm, v(-8.08, 87.67) * mm, v(-8.15, 87.66) * mm, v(-8.19, 87.65) * mm, v(-8.26, 87.63) * mm, v(-8.34, 87.6) * mm, v(-8.46, 87.54) * mm, v(-8.53, 87.5) * mm, v(-8.8, 87.32) * mm, v(-8.98, 87.12) * mm, v(-9.1, 86.93) * mm, v(-9.21, 86.73) * mm, v(-9.27, 86.62) * mm, v(-9.31, 86.5) * mm, v(-9.36, 86.38) * mm, v(-9.42, 86.17) * mm, v(-9.42, 85.98) * mm, v(-9.46, 85.8) * mm, v(-9.44, 85.63) * mm, v(-9.42, 85.45) * mm, v(-9.37, 85.34) * mm, v(-9.3, 85.2) * mm, v(-9.2, 85.13) * mm, v(-9.17, 85.03) * mm, v(-9.1, 84.99) * mm, v(-8.93, 84.9) * mm, v(-8.83, 84.88) * mm, v(-8.75, 84.88) * mm, v(-8.61, 84.87) * mm, v(-8.47, 84.85) * mm, v(-8.4, 84.88) * mm, v(-8.24, 84.92) * mm, v(-8.15, 84.97) * mm, v(-8.05, 85.03) * mm, v(-8.04, 85.07) * mm, v(-7.94, 85.13) * mm, v(-7.88, 85.2) * mm, v(-7.82, 85.24) * mm, v(-7.75, 85.32) * mm, v(-7.66, 85.16) * mm, v(-7.64, 85.1) * mm, v(-7.54, 85.04) * mm, v(-7.54, 84.95) * mm, v(-7.37, 84.91) * mm], "startDerivative": vector(-2.25, 4.56) * mm, "endDerivative": vector(9.47, -0.65) * mm});
            skFitSpline(sketch, "E24", {"points": [v(-7.37, 84.91) * mm, v(-7.25, 84.88) * mm, v(-7.17, 84.91) * mm, v(-7.08, 84.88) * mm, v(-7, 84.91) * mm, v(-6.9, 84.91) * mm, v(-6.86, 84.91) * mm, v(-6.8, 84.94) * mm, v(-6.76, 84.94) * mm, v(-6.68, 84.97) * mm, v(-6.59, 85) * mm, v(-6.55, 85.03) * mm, v(-6.5, 85.07) * mm, v(-6.45, 85.11) * mm, v(-6.41, 85.14) * mm, v(-6.36, 85.18) * mm, v(-6.31, 85.22) * mm, v(-6.27, 85.26) * mm, v(-6.2, 85.32) * mm, v(-6.14, 85.37) * mm, v(-6.09, 85.42) * mm, v(-6.05, 85.45) * mm, v(-6, 85.52) * mm, v(-5.95, 85.58) * mm, v(-5.89, 85.65) * mm, v(-5.8, 85.69) * mm, v(-5.77, 85.69) * mm, v(-5.78, 85.59) * mm, v(-5.8, 85.49) * mm, v(-5.83, 85.39) * mm, v(-5.84, 85.32) * mm, v(-5.87, 85.2) * mm, v(-5.9, 85.05) * mm, v(-5.93, 84.95) * mm, v(-5.96, 84.81) * mm, v(-6, 84.68) * mm, v(-6.02, 84.58) * mm], "startDerivative": vector(3.94, -1.7) * mm, "endDerivative": vector(-0.9, -3.12) * mm});
            skFitSpline(sketch, "E25", {"points": [v(-6.02, 84.58) * mm, v(-6.05, 84.48) * mm, v(-6.05, 84.41) * mm, v(-6.08, 84.38) * mm, v(-6.1, 84.34) * mm, v(-6.1, 84.3) * mm, v(-6.1, 84.28) * mm, v(-6.06, 84.27) * mm, v(-6.02, 84.27) * mm, v(-5.93, 84.27) * mm, v(-5.87, 84.26) * mm, v(-5.77, 84.27) * mm, v(-5.69, 84.25) * mm, v(-5.65, 84.25) * mm, v(-5.6, 84.25) * mm, v(-5.55, 84.26) * mm, v(-5.53, 84.26) * mm, v(-5.5, 84.35) * mm, v(-5.47, 84.46) * mm, v(-5.45, 84.55) * mm, v(-5.44, 84.63) * mm, v(-5.4, 84.74) * mm, v(-5.4, 84.81) * mm, v(-5.39, 84.88) * mm, v(-5.38, 84.96) * mm, v(-5.36, 84.96) * mm, v(-5.35, 85) * mm, v(-5.27, 85) * mm, v(-5.2, 84.96) * mm, v(-5.16, 84.91) * mm, v(-5.1, 84.91) * mm, v(-5.04, 84.88) * mm, v(-5, 84.88) * mm, v(-4.9, 84.87) * mm, v(-4.8, 84.88) * mm], "startDerivative": vector(-1.2, -2.57) * mm, "endDerivative": vector(2.5, 0.3) * mm});
            skFitSpline(sketch, "E26", {"points": [v(-4.8, 84.88) * mm, v(-4.7, 84.9) * mm, v(-4.63, 84.95) * mm, v(-4.57, 84.97) * mm, v(-4.47, 85.04) * mm, v(-4.43, 85.07) * mm, v(-4.36, 85.1) * mm, v(-4.3, 85.19) * mm, v(-4.25, 85.21) * mm, v(-4.18, 85.29) * mm, v(-4.12, 85.32) * mm, v(-4.08, 85.35) * mm, v(-4.02, 85.42) * mm, v(-3.94, 85.47) * mm, v(-3.92, 85.53) * mm, v(-3.86, 85.59) * mm, v(-3.81, 85.64) * mm, v(-3.75, 85.68) * mm, v(-3.7, 85.7) * mm, v(-3.68, 85.7) * mm, v(-3.64, 85.6) * mm, v(-3.64, 85.48) * mm, v(-3.64, 85.44) * mm, v(-3.64, 85.35) * mm, v(-3.63, 85.26) * mm, v(-3.61, 85.18) * mm, v(-3.59, 85.13) * mm, v(-3.54, 85.06) * mm, v(-3.5, 85) * mm, v(-3.43, 84.96) * mm, v(-3.39, 84.93) * mm, v(-3.3, 84.9) * mm, v(-3.18, 84.83) * mm, v(-3.1, 84.82) * mm, v(-2.99, 84.83) * mm, v(-2.92, 84.85) * mm, v(-2.86, 84.88) * mm, v(-2.77, 84.88) * mm, v(-2.7, 84.94) * mm, v(-2.64, 84.96) * mm, v(-2.57, 85.01) * mm, v(-2.5, 85.06) * mm, v(-2.42, 85.11) * mm, v(-2.35, 85.16) * mm, v(-2.32, 85.2) * mm, v(-2.24, 85.27) * mm, v(-2.19, 85.3) * mm, v(-2.17, 85.34) * mm, v(-2.14, 85.4) * mm, v(-2.09, 85.42) * mm, v(-2.06, 85.35) * mm, v(-2.03, 85.24) * mm, v(-2, 85.15) * mm, v(-1.97, 85.09) * mm, v(-1.94, 85.04) * mm, v(-1.89, 84.99) * mm], "startDerivative": vector(5.22, -0.09) * mm, "endDerivative": vector(3, -3.35) * mm});
            skFitSpline(sketch, "E27", {"points": [v(-1.89, 84.99) * mm, v(-1.81, 84.93) * mm, v(-1.8, 84.93) * mm, v(-1.75, 84.9) * mm, v(-1.68, 84.88) * mm, v(-1.63, 84.86) * mm, v(-1.6, 84.86) * mm, v(-1.52, 84.85) * mm, v(-1.48, 84.84) * mm, v(-1.4, 84.83) * mm, v(-1.32, 84.86) * mm, v(-1.25, 84.88) * mm, v(-1.18, 84.88) * mm, v(-1.1, 84.88) * mm, v(-1.03, 84.92) * mm, v(-0.96, 84.99) * mm, v(-0.9, 84.99) * mm, v(-0.84, 85.07) * mm, v(-0.76, 85.1) * mm, v(-0.74, 85.13) * mm, v(-0.7, 85.17) * mm, v(-0.67, 85.21) * mm, v(-0.64, 85.24) * mm, v(-0.59, 85.28) * mm, v(-0.55, 85.35) * mm, v(-0.5, 85.39) * mm, v(-0.5, 85.45) * mm, v(-0.46, 85.5) * mm, v(-0.42, 85.55) * mm, v(-0.39, 85.68) * mm, v(-0.35, 85.76) * mm, v(-0.35, 85.9) * mm, v(-0.35, 86.01) * mm, v(-0.35, 86.06) * mm, v(-0.35, 86.18) * mm, v(-0.38, 86.37) * mm, v(-0.44, 86.42) * mm, v(-0.46, 86.49) * mm, v(-0.5, 86.55) * mm, v(-0.54, 86.6) * mm, v(-0.57, 86.62) * mm, v(-0.62, 86.66) * mm, v(-0.66, 86.73) * mm, v(-0.7, 86.75) * mm, v(-0.78, 86.76) * mm, v(-0.84, 86.76) * mm, v(-0.89, 86.77) * mm, v(-0.93, 86.8) * mm, v(-1.03, 86.8) * mm, v(-1.07, 86.76) * mm, v(-1.1, 86.75) * mm, v(-1.18, 86.73) * mm, v(-1.23, 86.71) * mm, v(-1.3, 86.68) * mm, v(-1.35, 86.66) * mm], "startDerivative": vector(4.68, -2.94) * mm, "endDerivative": vector(-3.4, -0.4) * mm});
            skFitSpline(sketch, "E28", {"points": [v(-1.35, 86.66) * mm, v(-1.46, 86.58) * mm, v(-1.54, 86.52) * mm, v(-1.58, 86.47) * mm, v(-1.62, 86.44) * mm, v(-1.65, 86.4) * mm, v(-1.7, 86.36) * mm, v(-1.77, 86.28) * mm, v(-1.8, 86.24) * mm, v(-1.83, 86.19) * mm, v(-1.89, 86.14) * mm, v(-1.89, 86.09) * mm, v(-1.94, 86.03) * mm, v(-1.96, 85.98) * mm, v(-2.01, 85.9) * mm, v(-2.05, 85.84) * mm, v(-2.1, 85.76) * mm, v(-2.14, 85.71) * mm, v(-2.18, 85.66) * mm, v(-2.25, 85.6) * mm, v(-2.3, 85.55) * mm, v(-2.33, 85.5) * mm, v(-2.39, 85.45) * mm, v(-2.45, 85.39) * mm, v(-2.5, 85.3) * mm, v(-2.55, 85.3) * mm, v(-2.58, 85.27) * mm, v(-2.63, 85.23) * mm, v(-2.66, 85.2) * mm, v(-2.7, 85.2) * mm, v(-2.76, 85.18) * mm, v(-2.83, 85.17) * mm, v(-2.87, 85.18) * mm, v(-2.91, 85.18) * mm, v(-2.94, 85.2) * mm, v(-2.96, 85.21) * mm, v(-2.99, 85.25) * mm, v(-3, 85.26) * mm, v(-3.02, 85.29) * mm, v(-3.04, 85.32) * mm, v(-3.06, 85.35) * mm, v(-3.08, 85.4) * mm, v(-3.1, 85.48) * mm, v(-3.1, 85.55) * mm, v(-3.09, 85.64) * mm, v(-3.08, 85.69) * mm, v(-3.08, 85.78) * mm, v(-3.08, 85.82) * mm, v(-3.06, 85.86) * mm, v(-3.05, 85.96) * mm, v(-3.02, 86.03) * mm, v(-3.01, 86.09) * mm, v(-2.98, 86.15) * mm, v(-2.96, 86.2) * mm, v(-2.92, 86.24) * mm, v(-2.88, 86.3) * mm, v(-2.84, 86.35) * mm, v(-2.82, 86.4) * mm, v(-2.77, 86.46) * mm, v(-2.74, 86.48) * mm, v(-2.67, 86.53) * mm, v(-2.62, 86.55) * mm, v(-2.55, 86.56) * mm, v(-2.53, 86.56) * mm, v(-2.47, 86.54) * mm, v(-2.45, 86.53) * mm, v(-2.42, 86.49) * mm, v(-2.38, 86.44) * mm, v(-2.38, 86.41) * mm, v(-2.42, 86.4) * mm, v(-2.46, 86.4) * mm, v(-2.51, 86.39) * mm, v(-2.53, 86.38) * mm, v(-2.56, 86.36) * mm, v(-2.57, 86.34) * mm, v(-2.58, 86.3) * mm, v(-2.58, 86.27) * mm, v(-2.6, 86.2) * mm, v(-2.6, 86.16) * mm, v(-2.57, 86.1) * mm, v(-2.56, 86.07) * mm, v(-2.53, 86.03) * mm, v(-2.47, 86) * mm, v(-2.42, 86) * mm, v(-2.36, 85.99) * mm, v(-2.33, 85.99) * mm, v(-2.26, 85.99) * mm, v(-2.26, 86) * mm, v(-2.21, 86.02) * mm, v(-2.18, 86.06) * mm, v(-2.17, 86.1) * mm, v(-2.15, 86.12) * mm, v(-2.12, 86.16) * mm, v(-2.1, 86.22) * mm, v(-2.1, 86.3) * mm, v(-2.1, 86.4) * mm, v(-2.1, 86.47) * mm, v(-2.15, 86.52) * mm, v(-2.17, 86.55) * mm, v(-2.2, 86.62) * mm, v(-2.27, 86.66) * mm, v(-2.29, 86.69) * mm, v(-2.37, 86.73) * mm], "startDerivative": vector(-6.61, -6.1) * mm, "endDerivative": vector(-8.14, 3.13) * mm});
            skFitSpline(sketch, "E29", {"points": [v(-2.37, 86.73) * mm, v(-2.44, 86.76) * mm, v(-2.5, 86.77) * mm, v(-2.55, 86.77) * mm, v(-2.6, 86.77) * mm, v(-2.65, 86.78) * mm, v(-2.73, 86.77) * mm, v(-2.77, 86.76) * mm, v(-2.84, 86.73) * mm, v(-2.88, 86.73) * mm, v(-2.94, 86.68) * mm, v(-3, 86.66) * mm, v(-3.07, 86.61) * mm, v(-3.1, 86.58) * mm, v(-3.15, 86.54) * mm, v(-3.22, 86.47) * mm, v(-3.26, 86.45) * mm, v(-3.3, 86.4) * mm, v(-3.36, 86.34) * mm, v(-3.4, 86.3) * mm, v(-3.46, 86.22) * mm, v(-3.5, 86.18) * mm, v(-3.55, 86.12) * mm, v(-3.6, 86.06) * mm, v(-3.66, 86) * mm, v(-3.74, 85.94) * mm, v(-3.78, 85.89) * mm, v(-3.84, 85.84) * mm, v(-3.89, 85.8) * mm, v(-3.92, 85.77) * mm, v(-3.94, 85.74) * mm, v(-3.99, 85.74) * mm, v(-4, 85.77) * mm, v(-4, 85.83) * mm, v(-3.99, 85.91) * mm, v(-3.98, 85.98) * mm, v(-3.97, 86.06) * mm, v(-3.96, 86.16) * mm, v(-3.97, 86.21) * mm, v(-3.97, 86.27) * mm, v(-4, 86.34) * mm, v(-4, 86.44) * mm, v(-4.03, 86.47) * mm, v(-4.08, 86.54) * mm, v(-4.14, 86.58) * mm, v(-4.2, 86.64) * mm, v(-4.24, 86.66) * mm, v(-4.3, 86.66) * mm, v(-4.33, 86.72) * mm, v(-4.38, 86.72) * mm, v(-4.43, 86.72) * mm, v(-4.49, 86.72) * mm, v(-4.52, 86.72) * mm, v(-4.57, 86.72) * mm, v(-4.64, 86.72) * mm, v(-4.7, 86.66) * mm, v(-4.76, 86.66) * mm, v(-4.84, 86.64) * mm, v(-4.86, 86.61) * mm, v(-4.9, 86.58) * mm, v(-4.9, 86.6) * mm, v(-4.93, 86.63) * mm, v(-4.94, 86.66) * mm, v(-4.94, 86.7) * mm, v(-4.95, 86.72) * mm, v(-5, 86.72) * mm, v(-5.06, 86.72) * mm, v(-5.1, 86.72) * mm, v(-5.25, 86.73) * mm, v(-5.32, 86.73) * mm, v(-5.37, 86.73) * mm, v(-5.5, 86.73) * mm, v(-5.59, 86.73) * mm, v(-5.65, 86.73) * mm], "startDerivative": vector(-4.64, 1.85) * mm, "endDerivative": vector(-4.38, 0) * mm});
            skFitSpline(sketch, "E30", {"points": [v(-5.65, 86.73) * mm, v(-5.7, 86.73) * mm, v(-5.72, 86.73) * mm, v(-5.73, 86.73) * mm, v(-5.75, 86.66) * mm, v(-5.75, 86.6) * mm, v(-5.75, 86.58) * mm, v(-5.75, 86.58) * mm, v(-5.75, 86.55) * mm, v(-5.7, 86.54) * mm, v(-5.65, 86.54) * mm, v(-5.63, 86.53) * mm, v(-5.57, 86.53) * mm, v(-5.56, 86.52) * mm, v(-5.56, 86.47) * mm, v(-5.6, 86.47) * mm, v(-5.6, 86.45) * mm, v(-5.6, 86.38) * mm, v(-5.63, 86.34) * mm, v(-5.65, 86.3) * mm, v(-5.65, 86.26) * mm, v(-5.68, 86.23) * mm, v(-5.72, 86.17) * mm, v(-5.75, 86.1) * mm, v(-5.78, 86.08) * mm, v(-5.8, 86.04) * mm, v(-5.82, 86) * mm, v(-5.86, 85.95) * mm, v(-5.89, 85.92) * mm, v(-5.9, 85.9) * mm, v(-5.95, 85.85) * mm, v(-6, 85.8) * mm, v(-6, 85.8) * mm, v(-6.03, 85.78) * mm, v(-6.06, 85.77) * mm, v(-6.06, 85.83) * mm, v(-6.05, 85.9) * mm, v(-6.05, 85.95) * mm, v(-6.06, 86) * mm, v(-6.04, 86.07) * mm, v(-6.05, 86.13) * mm, v(-6.06, 86.2) * mm, v(-6.06, 86.25) * mm, v(-6.06, 86.3) * mm, v(-6.07, 86.34) * mm, v(-6.09, 86.4) * mm, v(-6.11, 86.45) * mm, v(-6.13, 86.47) * mm, v(-6.18, 86.55) * mm, v(-6.19, 86.58) * mm, v(-6.23, 86.63) * mm, v(-6.27, 86.66) * mm, v(-6.3, 86.66) * mm, v(-6.34, 86.72) * mm, v(-6.37, 86.72) * mm, v(-6.46, 86.77) * mm, v(-6.52, 86.78) * mm, v(-6.59, 86.8) * mm, v(-6.7, 86.8) * mm, v(-6.73, 86.78) * mm, v(-6.77, 86.76) * mm, v(-6.82, 86.76) * mm, v(-6.89, 86.73) * mm, v(-6.96, 86.72) * mm, v(-7, 86.66) * mm, v(-7.03, 86.64) * mm, v(-7.1, 86.58) * mm, v(-7.14, 86.58) * mm, v(-7.17, 86.53) * mm, v(-7.2, 86.47) * mm, v(-7.22, 86.47) * mm, v(-7.26, 86.4) * mm, v(-7.33, 86.34) * mm, v(-7.34, 86.34) * mm, v(-7.4, 86.3) * mm, v(-7.4, 86.25) * mm, v(-7.48, 86.18) * mm, v(-7.5, 86.14) * mm, v(-7.53, 86.12) * mm, v(-7.56, 86.07) * mm, v(-7.61, 86) * mm, v(-7.65, 85.96) * mm, v(-7.68, 85.89) * mm, v(-7.7, 85.85) * mm, v(-7.74, 85.79) * mm, v(-7.8, 85.72) * mm, v(-7.83, 85.66) * mm, v(-7.9, 85.59) * mm, v(-7.94, 85.53) * mm], "startDerivative": vector(-4.88, 0.08) * mm, "endDerivative": vector(-2.65, -4.34) * mm});
            skFitSpline(sketch, "E31", {"points": [v(-7.94, 85.53) * mm, v(-8, 85.47) * mm, v(-8.03, 85.44) * mm, v(-8.06, 85.4) * mm, v(-8.12, 85.35) * mm, v(-8.15, 85.33) * mm, v(-8.19, 85.3) * mm, v(-8.23, 85.26) * mm, v(-8.3, 85.22) * mm, v(-8.35, 85.2) * mm, v(-8.4, 85.21) * mm, v(-8.48, 85.2) * mm, v(-8.55, 85.22) * mm, v(-8.6, 85.23) * mm, v(-8.67, 85.27) * mm, v(-8.7, 85.3) * mm, v(-8.75, 85.36) * mm, v(-8.75, 85.43) * mm, v(-8.78, 85.53) * mm, v(-8.79, 85.59) * mm, v(-8.8, 85.69) * mm, v(-8.8, 85.8) * mm, v(-8.8, 85.84) * mm, v(-8.78, 85.98) * mm, v(-8.75, 86.04) * mm, v(-8.75, 86.1) * mm, v(-8.75, 86.19) * mm, v(-8.71, 86.3) * mm, v(-8.7, 86.37) * mm, v(-8.67, 86.47) * mm, v(-8.65, 86.5) * mm, v(-8.6, 86.61) * mm, v(-8.54, 86.7) * mm, v(-8.5, 86.79) * mm, v(-8.47, 86.85) * mm, v(-8.42, 86.91) * mm, v(-8.35, 87.04) * mm, v(-8.31, 87.09) * mm, v(-8.26, 87.15) * mm, v(-8.2, 87.24) * mm, v(-8.16, 87.27) * mm, v(-8.1, 87.3) * mm, v(-8.07, 87.33) * mm, v(-8.04, 87.35) * mm, v(-8, 87.35) * mm, v(-7.97, 87.37) * mm, v(-7.92, 87.36) * mm, v(-7.87, 87.36) * mm, v(-7.85, 87.36) * mm, v(-7.81, 87.35) * mm, v(-7.78, 87.35) * mm, v(-7.76, 87.33) * mm, v(-7.73, 87.28) * mm, v(-7.7, 87.23) * mm, v(-7.67, 87.15) * mm, v(-7.65, 87.1) * mm, v(-7.63, 87.04) * mm, v(-7.61, 86.97) * mm, v(-7.6, 86.9) * mm, v(-7.6, 86.81) * mm, v(-7.6, 86.78) * mm, v(-7.6, 86.73) * mm, v(-7.57, 86.72) * mm, v(-7.55, 86.72) * mm], "startDerivative": vector(-3.06, -3.8) * mm, "endDerivative": vector(2.32, -0.56) * mm});
            skFitSpline(sketch, "E32", {"points": [v(-6.65, 86.51) * mm, v(-6.72, 86.51) * mm, v(-6.74, 86.5) * mm, v(-6.82, 86.47) * mm, v(-6.87, 86.43) * mm, v(-6.9, 86.38) * mm, v(-6.95, 86.3) * mm, v(-6.98, 86.25) * mm, v(-7, 86.18) * mm, v(-7.02, 86.14) * mm, v(-7.06, 86.1) * mm, v(-7.08, 86.02) * mm, v(-7.11, 85.93) * mm, v(-7.12, 85.88) * mm, v(-7.14, 85.83) * mm, v(-7.16, 85.78) * mm, v(-7.18, 85.7) * mm, v(-7.2, 85.64) * mm, v(-7.23, 85.59) * mm, v(-7.23, 85.54) * mm, v(-7.23, 85.43) * mm, v(-7.23, 85.36) * mm, v(-7.2, 85.31) * mm, v(-7.2, 85.23) * mm, v(-7.2, 85.19) * mm, v(-7.17, 85.16) * mm, v(-7.15, 85.14) * mm, v(-7.13, 85.11) * mm, v(-7.08, 85.11) * mm, v(-7.03, 85.08) * mm, v(-6.98, 85.08) * mm, v(-6.92, 85.09) * mm, v(-6.89, 85.11) * mm, v(-6.84, 85.14) * mm, v(-6.78, 85.18) * mm, v(-6.75, 85.21) * mm, v(-6.71, 85.25) * mm, v(-6.68, 85.28) * mm, v(-6.65, 85.35) * mm, v(-6.62, 85.42) * mm, v(-6.6, 85.48) * mm, v(-6.58, 85.54) * mm, v(-6.55, 85.61) * mm, v(-6.53, 85.69) * mm, v(-6.52, 85.69) * mm, v(-6.5, 85.78) * mm, v(-6.48, 85.83) * mm, v(-6.47, 85.91) * mm, v(-6.46, 85.95) * mm, v(-6.44, 86.02) * mm, v(-6.44, 86.06) * mm, v(-6.45, 86.14) * mm, v(-6.46, 86.22) * mm, v(-6.45, 86.3) * mm, v(-6.45, 86.34) * mm, v(-6.46, 86.38) * mm, v(-6.47, 86.41) * mm, v(-6.5, 86.45) * mm, v(-6.52, 86.47) * mm, v(-6.57, 86.5) * mm, v(-6.65, 86.51) * mm]});
            skFitSpline(sketch, "E33", {"points": [v(-4.7, 86.47) * mm, v(-4.76, 86.47) * mm, v(-4.8, 86.47) * mm, v(-4.88, 86.44) * mm, v(-4.92, 86.41) * mm, v(-4.97, 86.34) * mm, v(-5, 86.3) * mm, v(-5.03, 86.21) * mm, v(-5.06, 86.14) * mm, v(-5.1, 86.08) * mm, v(-5.13, 85.96) * mm, v(-5.18, 85.84) * mm, v(-5.2, 85.78) * mm, v(-5.22, 85.67) * mm, v(-5.25, 85.59) * mm, v(-5.27, 85.45) * mm, v(-5.27, 85.38) * mm, v(-5.28, 85.32) * mm, v(-5.27, 85.24) * mm, v(-5.25, 85.2) * mm, v(-5.2, 85.16) * mm, v(-5.13, 85.11) * mm, v(-5.07, 85.11) * mm, v(-5.02, 85.11) * mm, v(-4.95, 85.11) * mm, v(-4.89, 85.15) * mm, v(-4.86, 85.2) * mm, v(-4.8, 85.24) * mm, v(-4.74, 85.3) * mm, v(-4.7, 85.38) * mm, v(-4.67, 85.44) * mm, v(-4.63, 85.53) * mm, v(-4.6, 85.59) * mm, v(-4.57, 85.66) * mm, v(-4.55, 85.78) * mm, v(-4.53, 85.84) * mm, v(-4.52, 85.93) * mm, v(-4.52, 86.02) * mm, v(-4.51, 86.08) * mm, v(-4.51, 86.14) * mm, v(-4.52, 86.3) * mm, v(-4.52, 86.34) * mm, v(-4.53, 86.4) * mm, v(-4.57, 86.43) * mm, v(-4.6, 86.47) * mm, v(-4.7, 86.47) * mm]});
            skFitSpline(sketch, "E34", {"points": [v(-0.98, 86.5) * mm, v(-1.07, 86.49) * mm, v(-1.12, 86.44) * mm, v(-1.14, 86.42) * mm, v(-1.18, 86.4) * mm, v(-1.22, 86.34) * mm, v(-1.26, 86.26) * mm, v(-1.29, 86.19) * mm, v(-1.33, 86.11) * mm, v(-1.38, 86.04) * mm, v(-1.4, 85.97) * mm, v(-1.43, 85.9) * mm, v(-1.46, 85.8) * mm, v(-1.47, 85.75) * mm, v(-1.5, 85.65) * mm, v(-1.5, 85.58) * mm, v(-1.54, 85.45) * mm, v(-1.54, 85.35) * mm, v(-1.5, 85.3) * mm, v(-1.5, 85.24) * mm, v(-1.5, 85.2) * mm, v(-1.4, 85.16) * mm, v(-1.3, 85.14) * mm, v(-1.27, 85.14) * mm, v(-1.2, 85.16) * mm, v(-1.14, 85.17) * mm, v(-1.08, 85.22) * mm, v(-1.04, 85.27) * mm, v(-1.01, 85.34) * mm, v(-0.97, 85.41) * mm, v(-0.93, 85.5) * mm, v(-0.91, 85.56) * mm, v(-0.89, 85.66) * mm, v(-0.85, 85.75) * mm, v(-0.82, 85.83) * mm, v(-0.8, 85.87) * mm, v(-0.8, 86.03) * mm, v(-0.78, 86.08) * mm, v(-0.78, 86.2) * mm, v(-0.77, 86.27) * mm, v(-0.79, 86.4) * mm, v(-0.81, 86.45) * mm, v(-0.87, 86.48) * mm, v(-0.98, 86.5) * mm]});
            skSolve(sketch);
        }
        {
            var Q0;
            Q0=makeQuery(id+"F6.imprint","IMPRINT",FACE,{"disambiguationData":[TD([[makeQuery(id+"F6.imprint","IMPRINT",EDGE,{"derivedFrom":sQuery(id+"F6.wireOp",EDGE,"E18")}),1.0]])]});
            var Q1;
            {var subQ4=sQuery(id+"F6.wireOp",EDGE,"E23");Q1=makeQuery(id+"F6.imprint","IMPRINT",FACE,{"disambiguationData":[TD([[makeQuery(id+"F6.imprint","IMPRINT",EDGE,{"derivedFrom":subQ4}),1.0]])]});}
            extrude(context, id + "F7", {"entities" : qUnion([Q0, Q1]), "operationType" : NewBodyOperationType.REMOVE, "oppositeDirection" : true, "depth" : 0.1 * mm, "offsetDistance" : 25 * mm});
        }
        {
            var Q0;
            Q0=qCreatedBy(makeId("Top.planeOp"),FACE);
            var sketch = newSketch(context, id + "F8", { "sketchPlane" : qUnion([Q0])});
            skLineSegment(sketch, "E35", {"start": v(-4, -51.22) * mm, "end": v(-4, -42.22) * mm});
            skLineSegment(sketch, "E36", {"start": v(-4, -42.22) * mm, "end": v(-5, -42.22) * mm});
            skLineSegment(sketch, "E37", {"start": v(-5, -42.22) * mm, "end": v(-5, -51.22) * mm});
            skLineSegment(sketch, "E38", {"start": v(-5, -51.22) * mm, "end": v(-4, -51.22) * mm});
            skLineSegment(sketch, "E39", {"start": v(-15.57, -51.22) * mm, "end": v(-15.57, -42.22) * mm});
            skLineSegment(sketch, "E40", {"start": v(-15.57, -42.22) * mm, "end": v(-14.57, -42.22) * mm});
            skLineSegment(sketch, "E41", {"start": v(-14.57, -42.22) * mm, "end": v(-14.57, -51.22) * mm});
            skLineSegment(sketch, "E42", {"start": v(-14.57, -51.22) * mm, "end": v(-15.57, -51.22) * mm});
            skSolve(sketch);
        }
        {
            var Q0;
            Q0=makeQuery(id+"F8.imprint","IMPRINT",FACE,{"disambiguationData":[TD([[makeQuery(id+"F8.imprint","IMPRINT",EDGE,{"derivedFrom":sQuery(id+"F8.wireOp",EDGE,"E39")}),-1.0]])]});
            var Q1;
            Q1=makeQuery(id+"F8.imprint","IMPRINT",FACE,{"disambiguationData":[TD([[makeQuery(id+"F8.imprint","IMPRINT",EDGE,{"derivedFrom":sQuery(id+"F8.wireOp",EDGE,"E35")}),1.0]])]});
            extrude(context, id + "F9", {"entities" : qUnion([Q0, Q1]), "operationType" : NewBodyOperationType.ADD, "depth" : 0.3 * mm, "offsetDistance" : 25 * mm});
        }
        {
            var Q0;
            Q0=makeQuery(id+"F9.opExtrude","CAP_FACE",FACE,{"disambiguationData":[OSD([sQuery(id+"F8.wireOp",EDGE,"E35"),sQuery(id+"F8.wireOp",EDGE,"E36"),sQuery(id+"F8.wireOp",EDGE,"E37"),sQuery(id+"F8.wireOp",EDGE,"E38")])],"isStart":false});
            var Q1;
            Q1=makeQuery(id+"F9.opExtrude","CAP_FACE",FACE,{"disambiguationData":[OSD([sQuery(id+"F8.wireOp",EDGE,"E39"),sQuery(id+"F8.wireOp",EDGE,"E40"),sQuery(id+"F8.wireOp",EDGE,"E41"),sQuery(id+"F8.wireOp",EDGE,"E42")])],"isStart":false});
            extrude(context, id + "F10", {"entities" : qUnion([Q0, Q1]), "operationType" : NewBodyOperationType.REMOVE, "oppositeDirection" : true, "depth" : 0.3 * mm, "offsetDistance" : 25 * mm});
        }
        {
            var Q0;
            {var subQ0=sQuery(id+"F0.wireOp",EDGE,"E0.bottom");var subQ1=sQuery(id+"F0.wireOp",EDGE,"E0.right");var subQ2=sQuery(id+"F0.wireOp",EDGE,"E0.left");Q0=makeQuery(id+"F3.boolean.opBoolean","SPLIT",FACE,{"disambiguationData":[TD([makeQuery(id+"F1.opExtrude","SWEPT_FACE",FACE,{"disambiguationData":[OSD([subQ0])]})])],"derivedFrom":makeQuery(id+"F1.opExtrude","CAP_FACE",FACE,{"disambiguationData":[OSD([subQ0,sQuery(id+"F0.wireOp",EDGE,"E0.top"),subQ2,subQ1])],"isStart":false})});}
            var sketch = newSketch(context, id + "F11", { "sketchPlane" : qUnion([Q0])});
            skLineSegment(sketch, "E43.bottom", {"start": v(-12.67, -33.23) * mm, "end": v(-6.67, -33.23) * mm});
            skLineSegment(sketch, "E43.top", {"start": v(-12.67, -21.23) * mm, "end": v(-6.67, -21.23) * mm});
            skLineSegment(sketch, "E43.left", {"start": v(-12.67, -33.23) * mm, "end": v(-12.67, -21.23) * mm});
            skLineSegment(sketch, "E43.right", {"start": v(-6.67, -33.23) * mm, "end": v(-6.67, -21.23) * mm});
            skSolve(sketch);
        }
        {
            var Q0;
            Q0=makeQuery(id+"F11.imprint","IMPRINT",FACE,{"disambiguationData":[TD([[makeQuery(id+"F11.imprint","IMPRINT",EDGE,{"derivedFrom":sQuery(id+"F11.wireOp",EDGE,"E43.bottom")}),1.0]])]});
            extrude(context, id + "F12", {"entities" : qUnion([Q0]), "operationType" : NewBodyOperationType.REMOVE, "oppositeDirection" : true, "depth" : 0.1 * mm, "offsetDistance" : 25 * mm});
        }
        {
            var Q0;
            Q0=makeQuery(id+"F12.boolean.opBoolean","COPY",FACE,{"derivedFrom":makeQuery(id+"F12.opExtrude","CAP_FACE",FACE,{"disambiguationData":[OSD([sQuery(id+"F11.wireOp",EDGE,"E43.bottom"),sQuery(id+"F11.wireOp",EDGE,"E43.top"),sQuery(id+"F11.wireOp",EDGE,"E43.left"),sQuery(id+"F11.wireOp",EDGE,"E43.right")])],"isStart":false})});
            var sketch = newSketch(context, id + "F13", { "sketchPlane" : qUnion([Q0])});
            skCircle(sketch, "E44", {"center": v(-9.67, -31.03) * mm, "radius": 0.7 * mm});
            skCircle(sketch, "E45", {"center": v(-9.67, -28.83) * mm, "radius": 0.7 * mm});
            skCircle(sketch, "E46", {"center": v(-9.67, -25.63) * mm, "radius": 0.7 * mm});
            skCircle(sketch, "E47", {"center": v(-9.67, -23.43) * mm, "radius": 0.7 * mm});
            skSolve(sketch);
        }
        {
            var Q0;
            Q0=makeQuery(id+"F13.imprint","IMPRINT",FACE,{"disambiguationData":[TD([[makeQuery(id+"F13.imprint","IMPRINT",EDGE,{"derivedFrom":sQuery(id+"F13.wireOp",EDGE,"E47")}),1.0]])]});
            var Q1;
            Q1=makeQuery(id+"F13.imprint","IMPRINT",FACE,{"disambiguationData":[TD([[makeQuery(id+"F13.imprint","IMPRINT",EDGE,{"derivedFrom":sQuery(id+"F13.wireOp",EDGE,"E46")}),1.0]])]});
            var Q2;
            Q2=makeQuery(id+"F13.imprint","IMPRINT",FACE,{"disambiguationData":[TD([[makeQuery(id+"F13.imprint","IMPRINT",EDGE,{"derivedFrom":sQuery(id+"F13.wireOp",EDGE,"E45")}),1.0]])]});
            var Q3;
            Q3=makeQuery(id+"F13.imprint","IMPRINT",FACE,{"disambiguationData":[TD([[makeQuery(id+"F13.imprint","IMPRINT",EDGE,{"derivedFrom":sQuery(id+"F13.wireOp",EDGE,"E44")}),1.0]])]});
            extrude(context, id + "F14", {"entities" : qUnion([Q0, Q1, Q2, Q3]), "operationType" : NewBodyOperationType.REMOVE, "oppositeDirection" : true, "depth" : 0.1 * mm, "offsetDistance" : 25 * mm});
        }
    });
